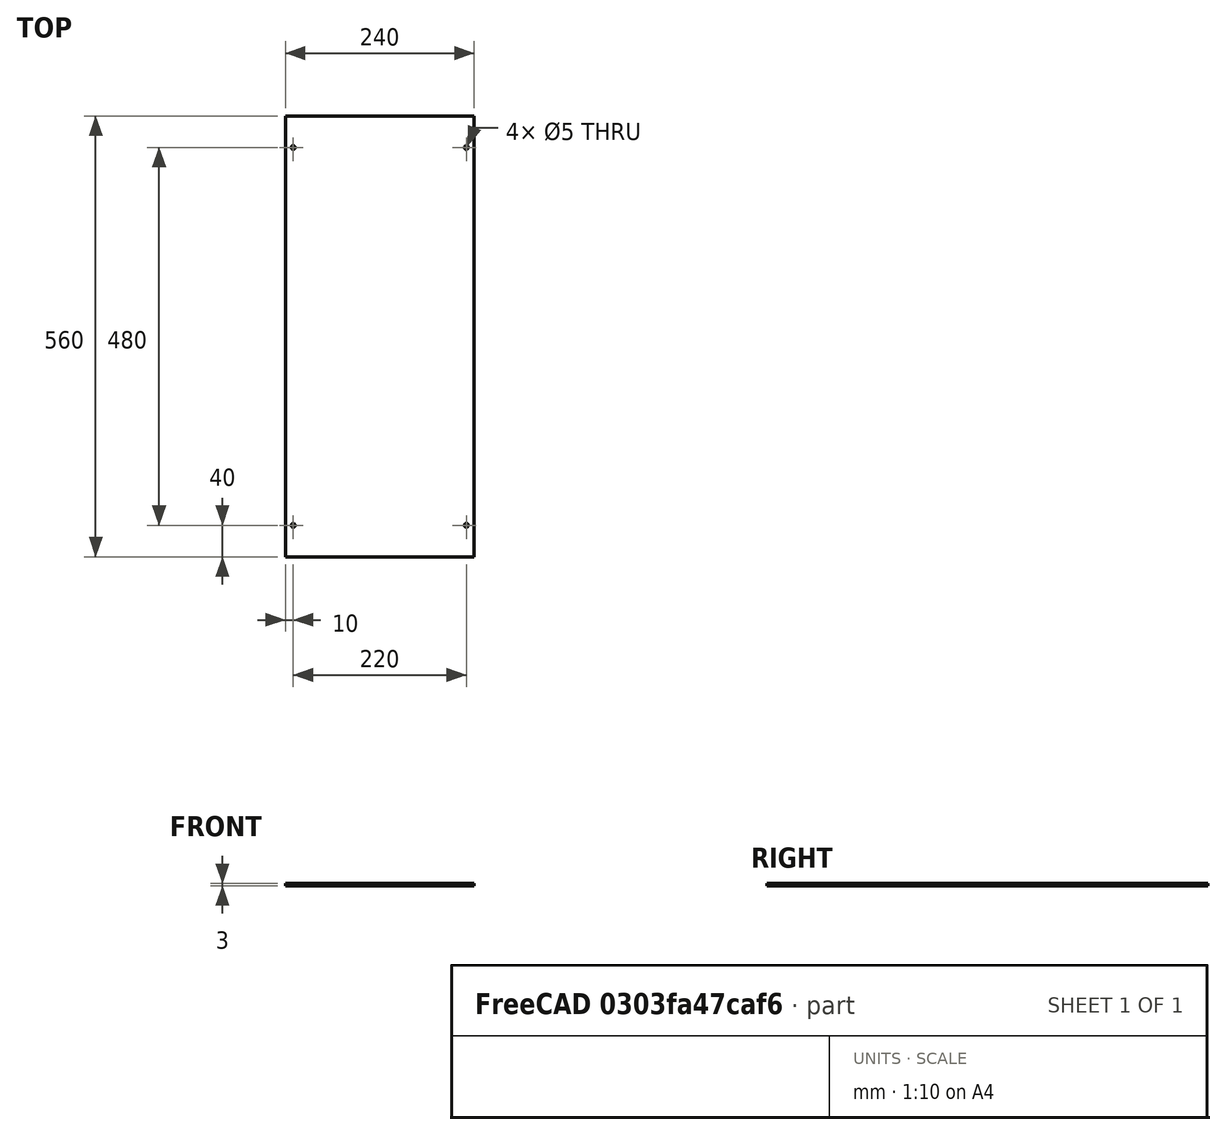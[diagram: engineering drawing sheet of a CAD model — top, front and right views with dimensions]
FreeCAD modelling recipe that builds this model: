
FCSTD DOCUMENT  (FreeCAD 1.0R38641 +468 (Git))
Label: plate_front_back
License: All rights reserved
LicenseURL: https://en.wikipedia.org/wiki/All_rights_reserved
objects: TechDraw::DrawViewDimension×7, TechDraw::DrawProjGroupItem×2, Sketcher::SketchObject×1, PartDesign::Pad×1, PartDesign::Body×1, TechDraw::DrawSVGTemplate×1, TechDraw::DrawProjGroup×1, TechDraw::DrawPage×1
note: 17 computed .brp shape members not serialized (recipe doc carries the construction recipe); baked Part::Feature solids carry a one-line shape summary decoded from their .brp

FEATURE [Sketcher::SketchObject] Sketch
  ArcFitTolerance = 1e-06
  AttachmentSupport = -> [XY_Plane]
  FullyConstrained = true
  MakeInternals = false
  MapMode = 5
  sketch-geometry (9):
    g0: LineSegment StartX=-120 StartY=280 StartZ=0 EndX=-120 EndY=-280 EndZ=0
    g1: LineSegment StartX=-120 StartY=-280 StartZ=0 EndX=120 EndY=-280 EndZ=0
    g2: LineSegment StartX=120 StartY=-280 StartZ=0 EndX=120 EndY=280 EndZ=0
    g3: LineSegment StartX=120 StartY=280 StartZ=0 EndX=-120 EndY=280 EndZ=0
    g4: GeomPoint [constr] X=0 Y=0 Z=0
    g5: Circle CenterX=-110 CenterY=240 CenterZ=0 NormalX=0 NormalY=0 NormalZ=1 AngleXU=0 Radius=2.5
    g6: Circle CenterX=110 CenterY=240 CenterZ=0 NormalX=0 NormalY=0 NormalZ=1 AngleXU=0 Radius=2.5
    g7: Circle CenterX=-110 CenterY=-240 CenterZ=0 NormalX=0 NormalY=0 NormalZ=1 AngleXU=0 Radius=2.5
    g8: Circle CenterX=110 CenterY=-240 CenterZ=0 NormalX=0 NormalY=0 NormalZ=1 AngleXU=0 Radius=2.5
  constraints (21):
    c: Coincident(g0,g1)
    c: Coincident(g1,g2)
    c: Coincident(g2,g3)
    c: Coincident(g3,g0)
    c: Vertical(g0)
    c: Vertical(g2)
    c: Horizontal(g1)
    c: Horizontal(g3)
    c: Symmetric(g2,g0,g4)
    c: Coincident(g4,g-1)
    c: DistanceX(g1,g1) = 240
    c: Distance(g0,g0) = 560
    c: Symmetric(g7,g8,g-2)
    c: Symmetric(g5,g6,g-2)
    c: Equal(g5,g6)
    c: Equal(g6,g7)
    c: Equal(g7,g8)
    c: Diameter(g5) = 5
    c: DistanceX(g5,g6) = 220
    c: Distance(g5,g3) = 40
    c: Symmetric(g7,g5,g-1)
FEATURE [PartDesign::Pad] Pad
  Direction = (0,0,1)
  Length = 3
  Length2 = 10
  Profile = -> Sketch
  ReferenceAxis = -> Sketch [N_Axis]
  Refine = true
  Suppressed = false
  Type = 0
FEATURE [PartDesign::Body] Body  label="plate_front_back"
  AllowCompound = false
  Group = -> [Sketch,Pad]
  Origin = -> Origin
  Tip = -> Pad
FEATURE [TechDraw::DrawSVGTemplate] Template
  EditableTexts = approval_person=B. Hecate; creator=Djordje Vujic; date_of_issue=20.1.25.; document_type=Assembly Drawing; general_tolerances=ISO 2768-m; identification_number=DN; language_code=EN; part_material=Stainless steel Mat.No. 1.4301; revision_index=AAA; sheet_number=1 / 1; sheet_scale=1 : 3; title=plate_front_back
  Height = 297
  Orientation = 0
  Template = /snap/freecad/1248/usr/share/Mod/TechDraw/Templates/A4_Portrait_ISO5457_minimal.svg
  Width = 210
FEATURE [TechDraw::DrawProjGroupItem] ProjItem  label="Front"
  CoarseView = false
  Direction = (0,0,1)
  Focus = 100
  HardHidden = false
  IsoCount = 0
  IsoHidden = false
  IsoVisible = false
  LockPosition = true
  Perspective = false
  Rotation = 0
  RotationVector = (1,0,0)
  Scale = 0.333333
  ScaleType = 0
  ScrubCount = 1
  SeamHidden = false
  SeamVisible = false
  SmoothHidden = false
  SmoothVisible = true
  Source = -> [Pad]
  Type = 0
  X = 0
  XDirection = (1,0,0)
  Y = 0
FEATURE [TechDraw::DrawProjGroupItem] ProjItem001  label="Bottom"
  CoarseView = false
  Direction = (0,-1,0)
  Focus = 100
  HardHidden = false
  IsoCount = 0
  IsoHidden = false
  IsoVisible = false
  LockPosition = false
  Perspective = false
  Rotation = 0
  RotationVector = (1,0,0)
  Scale = 0.333333
  ScaleType = 0
  ScrubCount = 1
  SeamHidden = false
  SeamVisible = false
  SmoothHidden = false
  SmoothVisible = true
  Source = -> [Pad]
  Type = 5
  X = 0
  XDirection = (1,0,0)
  Y = 108.833
FEATURE [TechDraw::DrawProjGroup] ProjGroup
  Anchor = -> ProjItem
  AutoDistribute = true
  LockPosition = false
  ProjectionType = 0
  Rotation = 0
  Scale = 0.333333
  ScaleType = 2
  Source = -> [Pad]
  Views = -> [ProjItem,ProjItem001]
  X = 108.714
  Y = 165.766
  spacingX = 15
  spacingY = 15
FEATURE [TechDraw::DrawViewDimension] Dimension
  AngleOverride = false
  Arbitrary = false
  ArbitraryTolerances = false
  BoxCorners = (2) [(-40,-93.3332,0),(40,93.3332,0)]
  EqualTolerance = true
  ExtensionAngle = 0
  FormatSpec = %.2w
  FormatSpecOverTolerance = %+.2w
  FormatSpecUnderTolerance = %+.2w
  Inverted = false
  LineAngle = 0
  LockPosition = false
  MeasureType = 1
  OverTolerance = 0
  References2D = -> [ProjItem]
  Rotation = 0
  ScaleType = 0
  TheoreticalExact = false
  Type = 2
  UnderTolerance = 0
  X = -65.5948
  Y = -13.6149
FEATURE [TechDraw::DrawViewDimension] Dimension001
  AngleOverride = false
  Arbitrary = false
  ArbitraryTolerances = false
  BoxCorners = (2) [(-40,-93.3332,0),(40,93.3332,0)]
  EqualTolerance = true
  ExtensionAngle = 0
  FormatSpec = %.2w
  FormatSpecOverTolerance = %+.2w
  FormatSpecUnderTolerance = %+.2w
  Inverted = false
  LineAngle = 0
  LockPosition = false
  MeasureType = 1
  OverTolerance = 0
  References2D = -> [ProjItem]
  Rotation = 0
  ScaleType = 0
  TheoreticalExact = false
  Type = 0
  UnderTolerance = 0
  X = 29.9466
  Y = -10.5485
FEATURE [TechDraw::DrawViewDimension] Dimension002
  AngleOverride = false
  Arbitrary = false
  ArbitraryTolerances = false
  BoxCorners = (2) [(-40,-93.3332,0),(40,93.3332,0)]
  EqualTolerance = true
  ExtensionAngle = 0
  FormatSpec = %.2w
  FormatSpecOverTolerance = %+.2w
  FormatSpecUnderTolerance = %+.2w
  Inverted = false
  LineAngle = 0
  LockPosition = false
  MeasureType = 1
  OverTolerance = 0
  References2D = -> [ProjItem]
  Rotation = 0
  ScaleType = 0
  TheoreticalExact = false
  Type = 0
  UnderTolerance = 0
  X = 0
  Y = 88.7319
FEATURE [TechDraw::DrawViewDimension] Dimension003
  AngleOverride = false
  Arbitrary = false
  ArbitraryTolerances = false
  BoxCorners = (2) [(-40,-0.5,0),(40,0.499999,0)]
  EqualTolerance = true
  ExtensionAngle = 0
  FormatSpec = %.2w
  FormatSpecOverTolerance = %+.2w
  FormatSpecUnderTolerance = %+.2w
  Inverted = false
  LineAngle = 0
  LockPosition = false
  MeasureType = 1
  OverTolerance = 0
  References2D = -> [ProjItem001]
  Rotation = 0
  ScaleType = 0
  TheoreticalExact = false
  Type = 1
  UnderTolerance = 0
  X = 0
  Y = -4.46495
FEATURE [TechDraw::DrawViewDimension] Dimension004
  AngleOverride = false
  Arbitrary = false
  ArbitraryTolerances = false
  BoxCorners = (2) [(-40,-93.3332,0),(40,93.3332,0)]
  EqualTolerance = true
  ExtensionAngle = 0
  FormatSpec = ⌀%.2w
  FormatSpecOverTolerance = %+.2w
  FormatSpecUnderTolerance = %+.2w
  Inverted = false
  LineAngle = 0
  LockPosition = false
  MeasureType = 1
  OverTolerance = 0
  References2D = -> [ProjItem]
  Rotation = 0
  ScaleType = 0
  TheoreticalExact = false
  Type = 5
  UnderTolerance = 0
  X = -31.0873
  Y = -86.6456
FEATURE [TechDraw::DrawViewDimension] Dimension005
  AngleOverride = false
  Arbitrary = false
  ArbitraryTolerances = false
  BoxCorners = (2) [(-40,-93.3332,0),(40,93.3332,0)]
  EqualTolerance = true
  ExtensionAngle = 0
  FormatSpec = %.2w
  FormatSpecOverTolerance = %+.2w
  FormatSpecUnderTolerance = %+.2w
  Inverted = false
  LineAngle = 0
  LockPosition = false
  MeasureType = 1
  OverTolerance = 0
  References2D = -> [ProjItem]
  Rotation = 0
  ScaleType = 0
  TheoreticalExact = false
  Type = 0
  UnderTolerance = 0
  X = 46.6848
  Y = 88.7319
FEATURE [TechDraw::DrawViewDimension] Dimension006
  AngleOverride = false
  Arbitrary = false
  ArbitraryTolerances = false
  BoxCorners = (2) [(-40,-93.3332,0),(40,93.3332,0)]
  EqualTolerance = true
  ExtensionAngle = 0
  FormatSpec = %.2w
  FormatSpecOverTolerance = %+.2w
  FormatSpecUnderTolerance = %+.2w
  Inverted = false
  LineAngle = 0
  LockPosition = false
  MeasureType = 1
  OverTolerance = 0
  References2D = -> [ProjItem]
  Rotation = 0
  ScaleType = 0
  TheoreticalExact = false
  Type = 0
  UnderTolerance = 0
  X = -48.2349
  Y = 86.6666
FEATURE [TechDraw::DrawPage] Page
  KeepUpdated = true
  NextBalloonIndex = 1
  ProjectionType = 0
  Template = -> Template
  Views = -> [ProjGroup,Dimension,Dimension001,Dimension002,Dimension003,Dimension004,Dimension005,Dimension006]
